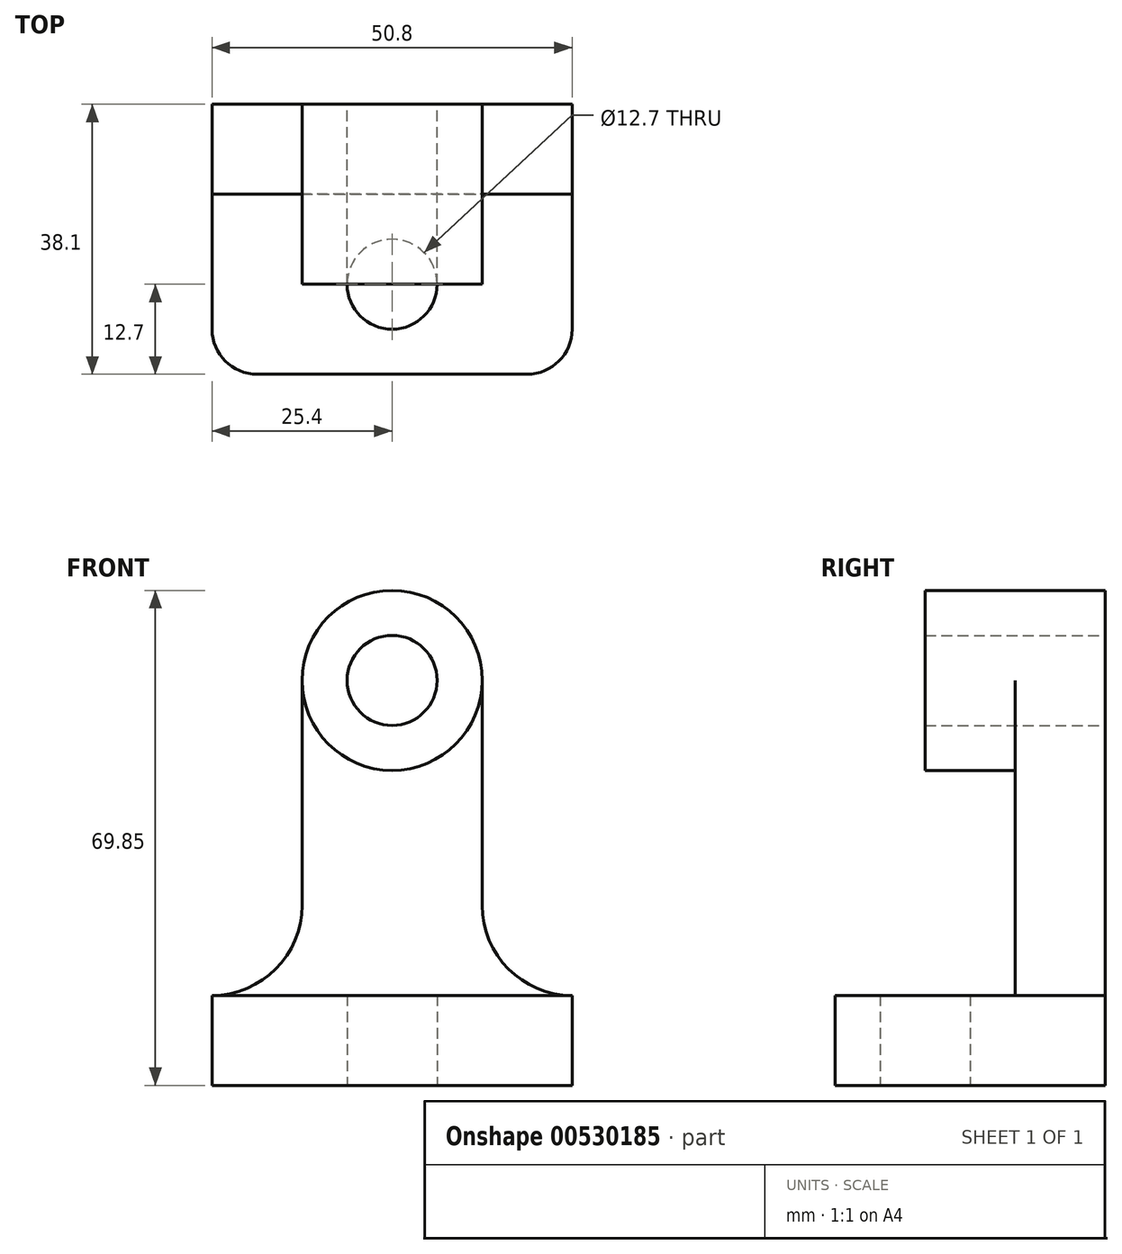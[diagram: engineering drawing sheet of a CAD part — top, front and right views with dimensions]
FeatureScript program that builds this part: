
annotation { "Feature Type Name" : "Feature", "Feature Type Description" : "" }
export const myFeature = defineFeature(function(context is Context, id is Id, definition is map)
    precondition{}
    {
        {
            var Q0;
            Q0=qCreatedBy(makeId("Front.planeOp"),FACE);
            var sketch = newSketch(context, id + "F0", { "sketchPlane" : qUnion([Q0])});
            skLineSegment(sketch, "E0", {"start": v(0, 0) * mm, "end": v(25.4, 0) * mm});
            skLineSegment(sketch, "E1", {"start": v(25.4, 0) * mm, "end": v(25.4, 12.7) * mm});
            skLineSegment(sketch, "E2", {"start": v(25.4, 12.7) * mm, "end": v(-25.4, 12.7) * mm});
            skLineSegment(sketch, "E3", {"start": v(-25.4, 12.7) * mm, "end": v(-25.4, 0) * mm});
            skLineSegment(sketch, "E4", {"start": v(-25.4, 0) * mm, "end": v(0, 0) * mm});
            skCircle(sketch, "E5", {"center": v(0, 57.15) * mm, "radius": 6.35 * mm});
            skCircle(sketch, "E6", {"center": v(0, 57.15) * mm, "radius": 12.7 * mm});
            skLineSegment(sketch, "E7", {"start": v(12.7, 57.15) * mm, "end": v(12.7, 25.4) * mm});
            skLineSegment(sketch, "E8", {"start": v(-12.7, 57.15) * mm, "end": v(-12.7, 25.4) * mm});
            skArc(sketch, "E9", {"start": v(12.7, 25.4) * mm, "mid": v(16.42, 16.42) * mm, "end": v(25.4, 12.7) * mm});
            skArc(sketch, "E10", {"start": v(-25.4, 12.7) * mm, "mid": v(-16.42, 16.42) * mm, "end": v(-12.7, 25.4) * mm});
            skSolve(sketch);
        }
        {
            var Q0;
            Q0=makeQuery(id+"F0.imprint","IMPRINT",FACE,{"disambiguationData":[TD([[makeQuery(id+"F0.imprint","IMPRINT",EDGE,{"derivedFrom":sQuery(id+"F0.wireOp",EDGE,"E2")}),-1.0]])]});
            extrude(context, id + "F1", {"entities" : qUnion([Q0]), "depth" : 12.7 * mm, "offsetDistance" : 25.4 * mm});
        }
        {
            var Q0;
            Q0=makeQuery(id+"F0.imprint","IMPRINT",FACE,{"disambiguationData":[TD([[makeQuery(id+"F0.imprint","IMPRINT",EDGE,{"derivedFrom":sQuery(id+"F0.wireOp",EDGE,"E5")}),-1.0]])]});
            extrude(context, id + "F2", {"entities" : qUnion([Q0]), "operationType" : NewBodyOperationType.ADD, "depth" : 25.4 * mm, "offsetDistance" : 25.4 * mm});
        }
        {
            var Q0;
            Q0=makeQuery(id+"F0.imprint","IMPRINT",FACE,{"disambiguationData":[TD([[makeQuery(id+"F0.imprint","IMPRINT",EDGE,{"derivedFrom":sQuery(id+"F0.wireOp",EDGE,"E0")}),1.0]])]});
            extrude(context, id + "F3", {"entities" : qUnion([Q0]), "operationType" : NewBodyOperationType.ADD, "depth" : 38.1 * mm, "offsetDistance" : 25.4 * mm});
        }
        {
            var Q0;
            Q0=makeQuery(id+"F3.opExtrude","CAP_EDGE",EDGE,{"disambiguationData":[OSD([sQuery(id+"F0.wireOp",EDGE,"E3")])],"isStart":false});
            var Q1;
            Q1=makeQuery(id+"F3.opExtrude","CAP_EDGE",EDGE,{"disambiguationData":[OSD([sQuery(id+"F0.wireOp",EDGE,"E1")])],"isStart":false});
            fillet(context, id + "F4", {"entities" : qUnion([Q0, Q1]), "radius" : 6.35 * mm, "tangentPropagation" : true, "allowEdgeOverflow" : false});
        }
        {
            var Q0;
            Q0=makeQuery(id+"F3.opExtrude","SWEPT_FACE",FACE,{"disambiguationData":[OSD([sQuery(id+"F0.wireOp",EDGE,"E0"),sQuery(id+"F0.wireOp",EDGE,"E4")])]});
            var sketch = newSketch(context, id + "F5", { "sketchPlane" : qUnion([Q0])});
            skCircle(sketch, "E11", {"center": v(0, 25.4) * mm, "radius": 6.35 * mm});
            skSolve(sketch);
        }
        {
            var Q0;
            Q0=makeQuery(id+"F5.imprint","IMPRINT",FACE,{"disambiguationData":[TD([[makeQuery(id+"F5.imprint","IMPRINT",EDGE,{"derivedFrom":sQuery(id+"F5.wireOp",EDGE,"E11")}),1.0]])]});
            extrude(context, id + "F6", {"entities" : qUnion([Q0]), "operationType" : NewBodyOperationType.REMOVE, "oppositeDirection" : true, "depth" : 25.4 * mm, "offsetDistance" : 25.4 * mm});
        }
    });
